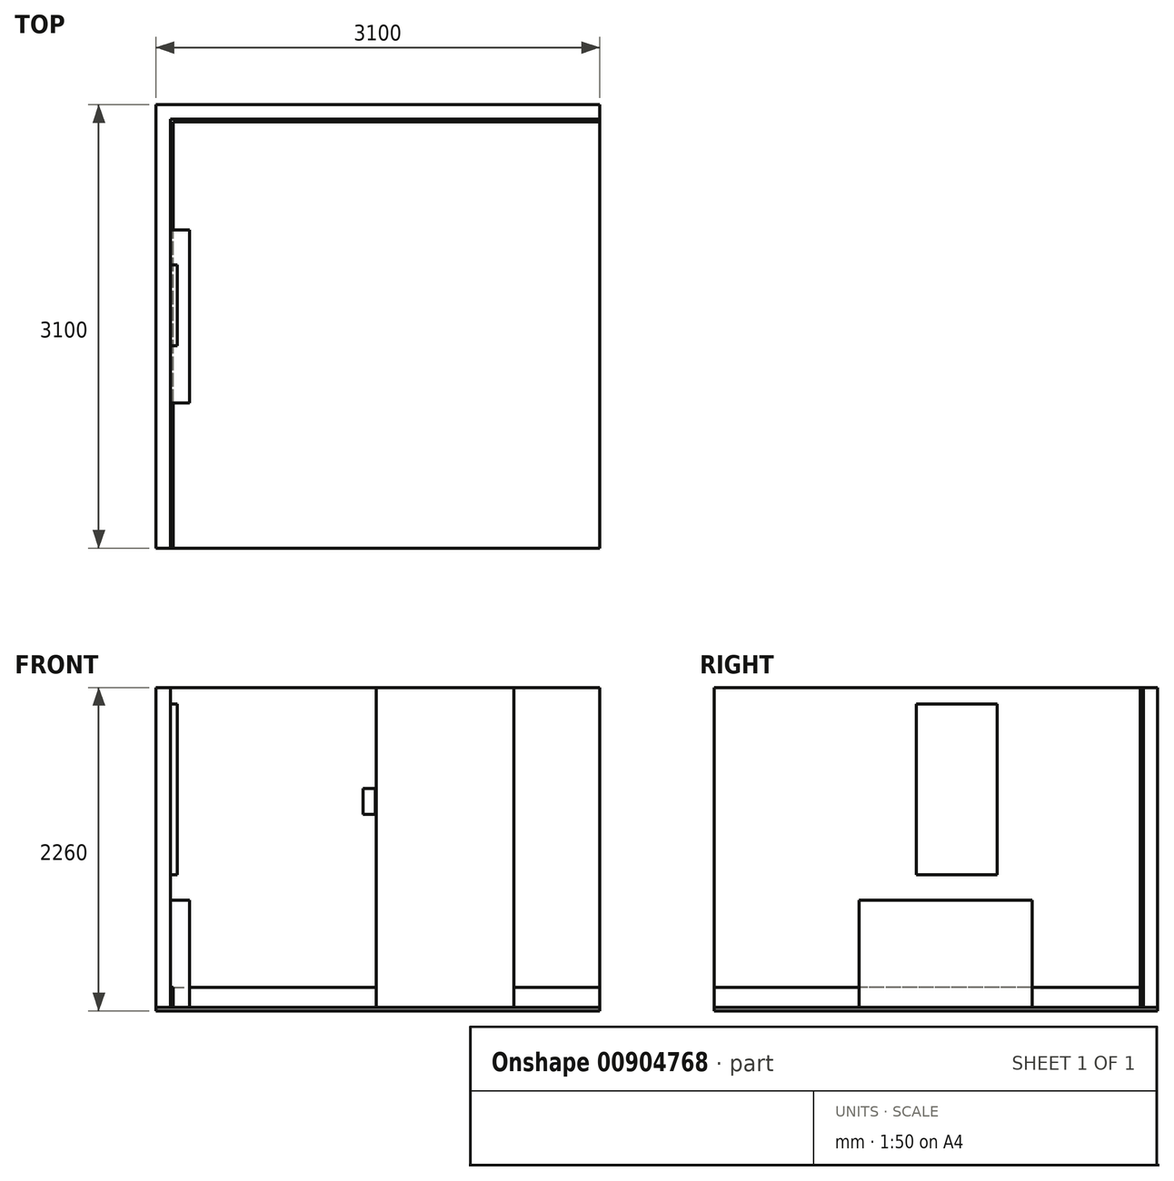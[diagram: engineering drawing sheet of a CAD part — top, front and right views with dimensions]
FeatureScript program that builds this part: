
annotation { "Feature Type Name" : "Feature", "Feature Type Description" : "" }
export const myFeature = defineFeature(function(context is Context, id is Id, definition is map)
    precondition{}
    {
        {
            var Q0;
            Q0=qCreatedBy(makeId("Top.planeOp"),FACE);
            var sketch = newSketch(context, id + "F0", { "sketchPlane" : qUnion([Q0])});
            skLineSegment(sketch, "E0", {"start": v(0, -3000) * mm, "end": v(0, 0) * mm});
            skLineSegment(sketch, "E1", {"start": v(0, 0) * mm, "end": v(3000, 0) * mm});
            skLineSegment(sketch, "E2", {"start": v(3000, 0) * mm, "end": v(3000, 100) * mm});
            skLineSegment(sketch, "E3", {"start": v(3000, 100) * mm, "end": v(-100, 100) * mm});
            skLineSegment(sketch, "E4", {"start": v(-100, 100) * mm, "end": v(-100, -3000) * mm});
            skLineSegment(sketch, "E5", {"start": v(-100, -3000) * mm, "end": v(0, -3000) * mm});
            skSolve(sketch);
        }
        {
            var Q0;
            Q0 = qSketchRegion(id + "F0", true);
            extrude(context, id + "F1", {"entities" : qUnion([Q0]), "depth" : 2235 * mm, "offsetDistance" : 25 * mm});
        }
        {
            var Q0;
            Q0=makeQuery(id+"F1.opExtrude","SWEPT_FACE",FACE,{"disambiguationData":[OSD([sQuery(id+"F0.wireOp",EDGE,"E1")])]});
            var sketch = newSketch(context, id + "F2", { "sketchPlane" : qUnion([Q0])});
            skLineSegment(sketch, "E6.bottom", {"start": v(1440, 0) * mm, "end": v(2400, 0) * mm});
            skLineSegment(sketch, "E6.top", {"start": v(1440, 2235) * mm, "end": v(2400, 2235) * mm});
            skLineSegment(sketch, "E6.left", {"start": v(1440, 0) * mm, "end": v(1440, 2235) * mm});
            skLineSegment(sketch, "E6.right", {"start": v(2400, 0) * mm, "end": v(2400, 2235) * mm});
            skSolve(sketch);
        }
        {
            var Q0;
            Q0 = qSketchRegion(id + "F2", true);
            extrude(context, id + "F3", {"entities" : qUnion([Q0]), "depth" : 20 * mm, "offsetDistance" : 25 * mm});
        }
        {
            var Q0;
            Q0=makeQuery(id+"F1.opExtrude","SWEPT_FACE",FACE,{"disambiguationData":[OSD([sQuery(id+"F0.wireOp",EDGE,"E0")])]});
            var sketch = newSketch(context, id + "F4", { "sketchPlane" : qUnion([Q0])});
            skLineSegment(sketch, "E7.bottom", {"start": v(-1985, 0) * mm, "end": v(-775, 0) * mm});
            skLineSegment(sketch, "E7.top", {"start": v(-1985, 750) * mm, "end": v(-775, 750) * mm});
            skLineSegment(sketch, "E7.left", {"start": v(-1985, 0) * mm, "end": v(-1985, 750) * mm});
            skLineSegment(sketch, "E7.right", {"start": v(-775, 0) * mm, "end": v(-775, 750) * mm});
            skSolve(sketch);
        }
        {
            var Q0;
            Q0 = qSketchRegion(id + "F4", true);
            extrude(context, id + "F5", {"entities" : qUnion([Q0]), "depth" : 135 * mm, "offsetDistance" : 25 * mm});
        }
        {
            var Q0;
            Q0=makeQuery(id+"F1.opExtrude","SWEPT_FACE",FACE,{"disambiguationData":[OSD([sQuery(id+"F0.wireOp",EDGE,"E0")])]});
            var sketch = newSketch(context, id + "F6", { "sketchPlane" : qUnion([Q0])});
            skLineSegment(sketch, "E8.bottom", {"start": v(-1585, 925) * mm, "end": v(-1020, 925) * mm});
            skLineSegment(sketch, "E8.top", {"start": v(-1585, 2120) * mm, "end": v(-1020, 2120) * mm});
            skLineSegment(sketch, "E8.left", {"start": v(-1585, 925) * mm, "end": v(-1585, 2120) * mm});
            skLineSegment(sketch, "E8.right", {"start": v(-1020, 925) * mm, "end": v(-1020, 2120) * mm});
            skSolve(sketch);
        }
        {
            var Q0;
            Q0 = qSketchRegion(id + "F6", true);
            extrude(context, id + "F7", {"entities" : qUnion([Q0]), "depth" : 50 * mm, "offsetDistance" : 25 * mm});
        }
        {
            var Q0;
            Q0=qCreatedBy(makeId("Top.planeOp"),FACE);
            var sketch = newSketch(context, id + "F8", { "sketchPlane" : qUnion([Q0])});
            skLineSegment(sketch, "E9", {"start": v(3000, 0) * mm, "end": v(0, 0) * mm});
            skLineSegment(sketch, "E10", {"start": v(0, 0) * mm, "end": v(0, -3000) * mm});
            skLineSegment(sketch, "E11", {"start": v(0, -3000) * mm, "end": v(20, -3000) * mm});
            skLineSegment(sketch, "E12", {"start": v(20, -3000) * mm, "end": v(20, -20) * mm});
            skLineSegment(sketch, "E13", {"start": v(20, -20) * mm, "end": v(3000, -20) * mm});
            skLineSegment(sketch, "E14", {"start": v(3000, -20) * mm, "end": v(3000, 0) * mm});
            skSolve(sketch);
        }
        {
            var Q0;
            Q0 = qSketchRegion(id + "F8", true);
            extrude(context, id + "F9", {"entities" : qUnion([Q0]), "depth" : 140 * mm, "offsetDistance" : 25 * mm});
        }
        {
            var Q0;
            Q0=makeQuery(id+"F9.opExtrude","SWEPT_BODY",BODY,{"disambiguationData":[OSD([sQuery(id+"F8.wireOp",EDGE,"E9"),sQuery(id+"F8.wireOp",EDGE,"E10"),sQuery(id+"F8.wireOp",EDGE,"E11"),sQuery(id+"F8.wireOp",EDGE,"E12"),sQuery(id+"F8.wireOp",EDGE,"E13"),sQuery(id+"F8.wireOp",EDGE,"E14")])]});
            var Q1;
            Q1=makeQuery(id+"F5.opExtrude","SWEPT_BODY",BODY,{"disambiguationData":[OSD([sQuery(id+"F4.wireOp",EDGE,"E7.bottom"),sQuery(id+"F4.wireOp",EDGE,"E7.top"),sQuery(id+"F4.wireOp",EDGE,"E7.left"),sQuery(id+"F4.wireOp",EDGE,"E7.right")])]});
            booleanBodies(context, id + "F10", {"operationType" : BooleanOperationType.SUBTRACTION, "tools" : qUnion([Q0]), "targets" : qUnion([Q1]), "keepTools" : true});
        }
        {
            var Q0;
            Q0=makeQuery(id+"F3.opExtrude","SWEPT_BODY",BODY,{"disambiguationData":[OSD([sQuery(id+"F2.wireOp",EDGE,"E6.bottom"),sQuery(id+"F2.wireOp",EDGE,"E6.top"),sQuery(id+"F2.wireOp",EDGE,"E6.left"),sQuery(id+"F2.wireOp",EDGE,"E6.right")])]});
            var Q1;
            Q1=makeQuery(id+"F9.opExtrude","SWEPT_BODY",BODY,{"disambiguationData":[OSD([sQuery(id+"F8.wireOp",EDGE,"E9"),sQuery(id+"F8.wireOp",EDGE,"E10"),sQuery(id+"F8.wireOp",EDGE,"E11"),sQuery(id+"F8.wireOp",EDGE,"E12"),sQuery(id+"F8.wireOp",EDGE,"E13"),sQuery(id+"F8.wireOp",EDGE,"E14")])]});
            booleanBodies(context, id + "F11", {"operationType" : BooleanOperationType.SUBTRACTION, "tools" : qUnion([Q0]), "targets" : qUnion([Q1]), "keepTools" : true});
        }
        {
            var Q0;
            Q0=makeQuery(id+"F1.opExtrude","SWEPT_FACE",FACE,{"disambiguationData":[OSD([sQuery(id+"F0.wireOp",EDGE,"E1")])]});
            var sketch = newSketch(context, id + "F12", { "sketchPlane" : qUnion([Q0])});
            skLineSegment(sketch, "E15.bottom", {"start": v(1432, 1530) * mm, "end": v(1347, 1530) * mm});
            skLineSegment(sketch, "E15.top", {"start": v(1432, 1350) * mm, "end": v(1347, 1350) * mm});
            skLineSegment(sketch, "E15.left", {"start": v(1432, 1530) * mm, "end": v(1432, 1350) * mm});
            skLineSegment(sketch, "E15.right", {"start": v(1347, 1530) * mm, "end": v(1347, 1350) * mm});
            skSolve(sketch);
        }
        {
            var Q0;
            Q0 = qSketchRegion(id + "F12", true);
            var Q1;
            Q1=makeQuery(id+"F3.opExtrude","CAP_FACE",FACE,{"disambiguationData":[OSD([sQuery(id+"F2.wireOp",EDGE,"E6.bottom"),sQuery(id+"F2.wireOp",EDGE,"E6.top"),sQuery(id+"F2.wireOp",EDGE,"E6.left"),sQuery(id+"F2.wireOp",EDGE,"E6.right")])],"isStart":false});
            extrude(context, id + "F13", {"entities" : qUnion([Q0]), "endBound" : BoundingType.UP_TO_SURFACE, "depth" : 25 * mm, "endBoundEntityFace" : qUnion([Q1]), "offsetDistance" : 25 * mm});
        }
        {
            var Q0;
            Q0=qCreatedBy(makeId("Top.planeOp"),FACE);
            var sketch = newSketch(context, id + "F14", { "sketchPlane" : qUnion([Q0])});
            skLineSegment(sketch, "E16.bottom", {"start": v(-100, 100) * mm, "end": v(3000, 100) * mm});
            skLineSegment(sketch, "E16.top", {"start": v(-100, -3000) * mm, "end": v(3000, -3000) * mm});
            skLineSegment(sketch, "E16.left", {"start": v(-100, 100) * mm, "end": v(-100, -3000) * mm});
            skLineSegment(sketch, "E16.right", {"start": v(3000, 100) * mm, "end": v(3000, -3000) * mm});
            skSolve(sketch);
        }
        {
            var Q0;
            Q0 = qSketchRegion(id + "F14", true);
            extrude(context, id + "F15", {"entities" : qUnion([Q0]), "oppositeDirection" : true, "depth" : 25 * mm, "offsetDistance" : 25 * mm});
        }
    });
